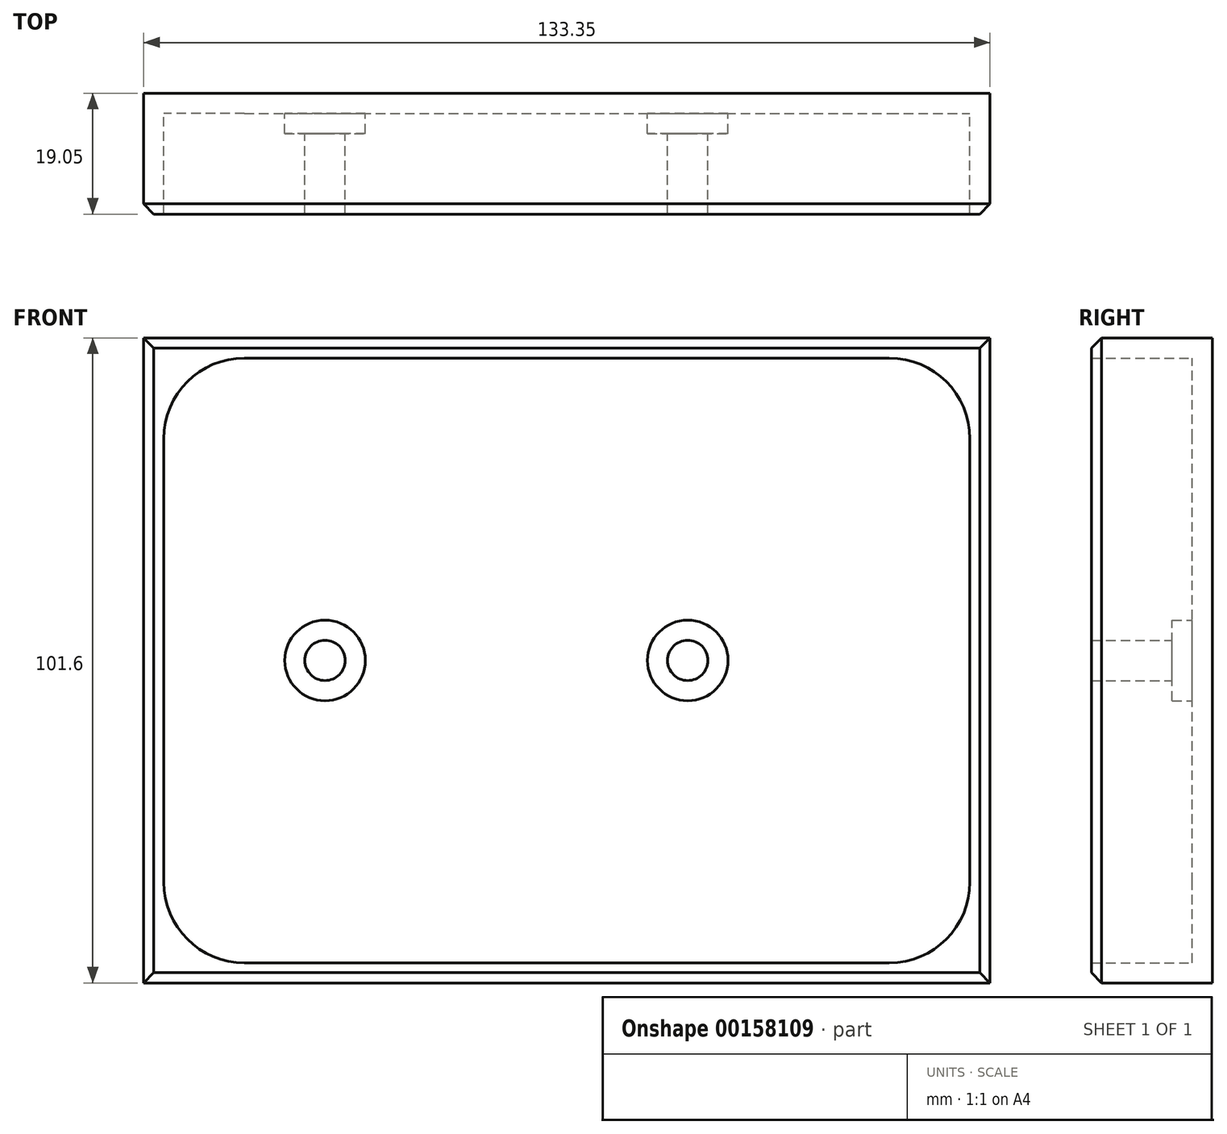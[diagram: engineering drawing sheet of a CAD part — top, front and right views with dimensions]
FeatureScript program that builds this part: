
annotation { "Feature Type Name" : "Feature", "Feature Type Description" : "" }
export const myFeature = defineFeature(function(context is Context, id is Id, definition is map)
    precondition{}
    {
        {
            var Q0;
            Q0=qCreatedBy(makeId("Front.planeOp"),FACE);
            var sketch = newSketch(context, id + "F0", { "sketchPlane" : qUnion([Q0])});
            skLineSegment(sketch, "E0.bottom", {"start": v(0, 13.2) * mm, "end": v(133.35, 13.2) * mm});
            skLineSegment(sketch, "E0.top", {"start": v(0, 114.8) * mm, "end": v(133.35, 114.8) * mm});
            skLineSegment(sketch, "E0.left", {"start": v(0, 13.2) * mm, "end": v(0, 114.8) * mm});
            skLineSegment(sketch, "E0.right", {"start": v(133.35, 13.2) * mm, "end": v(133.35, 114.8) * mm});
            skSolve(sketch);
        }
        {
            var Q0;
            Q0 = qSketchRegion(id + "F0", true);
            extrude(context, id + "F1", {"entities" : qUnion([Q0]), "depth" : 19.05 * mm});
        }
        {
            var Q0;
            Q0=makeQuery(id+"F1.opExtrude","CAP_FACE",FACE,{"disambiguationData":[OSD([sQuery(id+"F0.wireOp",EDGE,"E0.bottom"),sQuery(id+"F0.wireOp",EDGE,"E0.top"),sQuery(id+"F0.wireOp",EDGE,"E0.left"),sQuery(id+"F0.wireOp",EDGE,"E0.right")])],"isStart":false});
            shell(context, id + "F2", {"entities" : qUnion([Q0]), "thickness" : 3.17 * mm});
        }
        {
            var Q0;
            Q0=makeQuery(id+"F2.opShell","OFFSET_FACE",FACE,{"disambiguationData":[OSD([sQuery(id+"F0.wireOp",EDGE,"E0.bottom"),sQuery(id+"F0.wireOp",EDGE,"E0.top"),sQuery(id+"F0.wireOp",EDGE,"E0.left"),sQuery(id+"F0.wireOp",EDGE,"E0.right")])]});
            var sketch = newSketch(context, id + "F3", { "sketchPlane" : qUnion([Q0])});
            skCircle(sketch, "E1", {"center": v(28.58, 64) * mm, "radius": 6.35 * mm});
            skPoint(sketch, "E1.centerSnap0", {"position": v(3.17, 64) * mm});
            skCircle(sketch, "E2", {"center": v(85.73, 64) * mm, "radius": 6.35 * mm});
            skSolve(sketch);
        }
        {
            var Q0;
            Q0 = qSketchRegion(id + "F3", true);
            extrude(context, id + "F4", {"entities" : qUnion([Q0]), "operationType" : NewBodyOperationType.ADD, "depth" : 3.17 * mm});
        }
        {
            var Q0;
            Q0=makeQuery(id+"F4.opExtrude","CAP_FACE",FACE,{"disambiguationData":[OSD([sQuery(id+"F3.wireOp",EDGE,"E1")])],"isStart":false});
            var sketch = newSketch(context, id + "F5", { "sketchPlane" : qUnion([Q0])});
            skCircle(sketch, "E3", {"center": v(28.58, 64) * mm, "radius": 3.17 * mm});
            skSolve(sketch);
        }
        {
            var Q0;
            Q0 = qSketchRegion(id + "F5", true);
            extrude(context, id + "F6", {"entities" : qUnion([Q0]), "operationType" : NewBodyOperationType.ADD, "depth" : 12.7 * mm});
        }
        {
            var Q0;
            Q0=makeQuery(id+"F4.opExtrude","CAP_FACE",FACE,{"disambiguationData":[OSD([sQuery(id+"F3.wireOp",EDGE,"E2")])],"isStart":false});
            var sketch = newSketch(context, id + "F7", { "sketchPlane" : qUnion([Q0])});
            skCircle(sketch, "E4", {"center": v(85.73, 64) * mm, "radius": 3.18 * mm});
            skSolve(sketch);
        }
        {
            var Q0;
            Q0 = qSketchRegion(id + "F7", true);
            extrude(context, id + "F8", {"entities" : qUnion([Q0]), "operationType" : NewBodyOperationType.ADD, "depth" : 12.7 * mm});
        }
        {
            var Q0;
            Q0=makeQuery(id+"F2.opShell","OFFSET_EDGE",EDGE,{"disambiguationData":[OSD([sQuery(id+"F0.wireOp",EDGE,"E0.top"),sQuery(id+"F0.wireOp",EDGE,"E0.left")])]});
            var Q1;
            Q1=makeQuery(id+"F2.opShell","OFFSET_EDGE",EDGE,{"disambiguationData":[OSD([sQuery(id+"F0.wireOp",EDGE,"E0.bottom"),sQuery(id+"F0.wireOp",EDGE,"E0.left")])]});
            var Q2;
            Q2=makeQuery(id+"F2.opShell","OFFSET_EDGE",EDGE,{"disambiguationData":[OSD([sQuery(id+"F0.wireOp",EDGE,"E0.top"),sQuery(id+"F0.wireOp",EDGE,"E0.right")])]});
            var Q3;
            Q3=makeQuery(id+"F2.opShell","OFFSET_EDGE",EDGE,{"disambiguationData":[OSD([sQuery(id+"F0.wireOp",EDGE,"E0.bottom"),sQuery(id+"F0.wireOp",EDGE,"E0.right")])]});
            fillet(context, id + "F9", {"entities" : qUnion([Q0, Q1, Q2, Q3]), "radius" : 12.7 * mm, "tangentPropagation" : true, "allowEdgeOverflow" : false});
        }
        {
            var Q0;
            Q0=makeQuery(id+"F1.opExtrude","CAP_EDGE",EDGE,{"disambiguationData":[OSD([sQuery(id+"F0.wireOp",EDGE,"E0.top")])],"isStart":false});
            var Q1;
            Q1=makeQuery(id+"F1.opExtrude","CAP_EDGE",EDGE,{"disambiguationData":[OSD([sQuery(id+"F0.wireOp",EDGE,"E0.bottom")])],"isStart":false});
            var Q2;
            Q2=makeQuery(id+"F1.opExtrude","CAP_EDGE",EDGE,{"disambiguationData":[OSD([sQuery(id+"F0.wireOp",EDGE,"E0.right")])],"isStart":false});
            var Q3;
            Q3=makeQuery(id+"F1.opExtrude","CAP_EDGE",EDGE,{"disambiguationData":[OSD([sQuery(id+"F0.wireOp",EDGE,"E0.left")])],"isStart":false});
            chamfer(context, id + "F10", {"entities" : qUnion([Q0, Q1, Q2, Q3]), "width" : 1.6 * mm, "tangentPropagation" : true});
        }
    });
